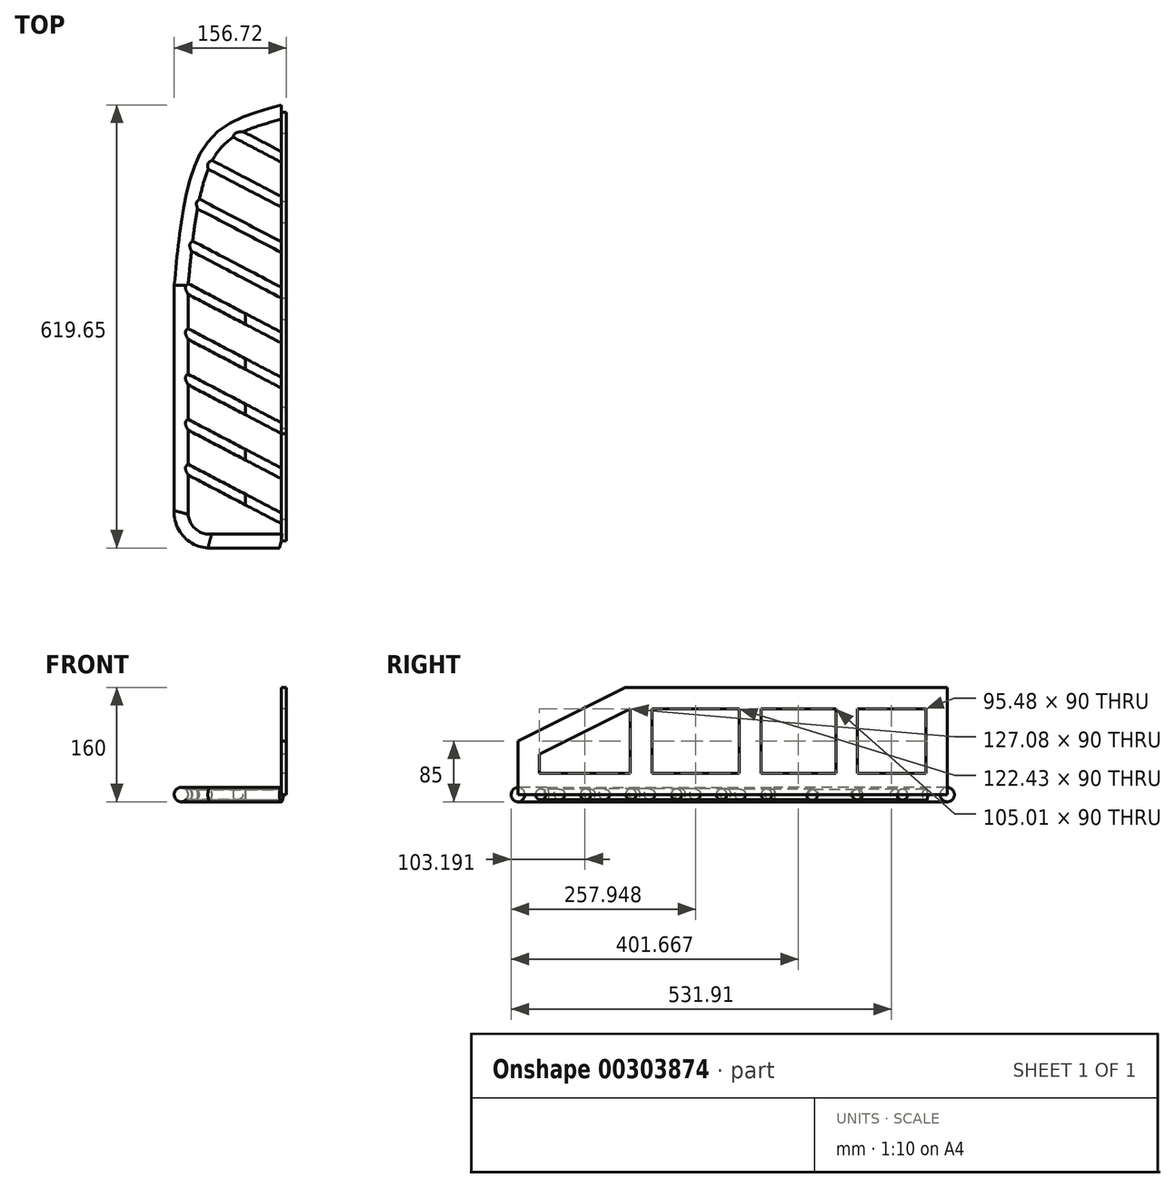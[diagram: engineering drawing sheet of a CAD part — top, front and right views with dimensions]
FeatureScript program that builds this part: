
annotation { "Feature Type Name" : "Feature", "Feature Type Description" : "" }
export const myFeature = defineFeature(function(context is Context, id is Id, definition is map)
    precondition{}
    {
        {
            var Q0;
            Q0=qCreatedBy(makeId("Right.planeOp"),FACE);
            var sketch = newSketch(context, id + "F0", { "sketchPlane" : qUnion([Q0])});
            skLineSegment(sketch, "E0.bottom", {"start": v(300, 75) * mm, "end": v(-150, 75) * mm});
            skLineSegment(sketch, "E0.top", {"start": v(300, -75) * mm, "end": v(-300, -75) * mm});
            skLineSegment(sketch, "E0.left", {"start": v(300, 75) * mm, "end": v(300, -75) * mm});
            skLineSegment(sketch, "E0.right", {"start": v(-300, 0) * mm, "end": v(-300, -75) * mm});
            skPoint(sketch, "E0.middle", {"position": v(0, 0) * mm});
            skLineSegment(sketch, "E1", {"start": v(-300, 0) * mm, "end": v(-150, 75) * mm});
            skLineSegment(sketch, "E2.0", {"start": v(-270, -18.54) * mm, "end": v(-142.92, 45) * mm});
            skLineSegment(sketch, "E2.1", {"start": v(270, 45) * mm, "end": v(174.52, 45) * mm});
            skLineSegment(sketch, "E2.2", {"start": v(-270, -18.54) * mm, "end": v(-270, -45) * mm});
            skLineSegment(sketch, "E2.3", {"start": v(270, -45) * mm, "end": v(174.52, -45) * mm});
            skLineSegment(sketch, "E2.4", {"start": v(270, 45) * mm, "end": v(270, -45) * mm});
            skLineSegment(sketch, "E3.left", {"start": v(-142.92, -45) * mm, "end": v(-142.92, 45) * mm});
            skLineSegment(sketch, "E3.right", {"start": v(-112.92, -45) * mm, "end": v(-112.92, 45) * mm});
            skLineSegment(sketch, "E4.left", {"start": v(9.51, -45) * mm, "end": v(9.51, 45) * mm});
            skLineSegment(sketch, "E4.right", {"start": v(39.51, -45) * mm, "end": v(39.51, 45) * mm});
            skLineSegment(sketch, "E5.left", {"start": v(144.52, 45) * mm, "end": v(144.52, -45) * mm});
            skLineSegment(sketch, "E5.right", {"start": v(174.52, 45) * mm, "end": v(174.52, -45) * mm});
            skLineSegment(sketch, "E6.trimOffspring", {"start": v(-142.92, -45) * mm, "end": v(-270, -45) * mm});
            skLineSegment(sketch, "E7.trimOffspring", {"start": v(9.51, -45) * mm, "end": v(-112.92, -45) * mm});
            skLineSegment(sketch, "E8.trimOffspring", {"start": v(9.51, 45) * mm, "end": v(-112.92, 45) * mm});
            skLineSegment(sketch, "E9.trimOffspring", {"start": v(144.52, 45) * mm, "end": v(39.51, 45) * mm});
            skLineSegment(sketch, "E10.trimOffspring", {"start": v(144.52, -45) * mm, "end": v(39.51, -45) * mm});
            skSolve(sketch);
        }
        {
            var Q0;
            Q0=makeQuery(id+"F0.imprint","IMPRINT",FACE,{"disambiguationData":[TD([[makeQuery(id+"F0.imprint","IMPRINT",EDGE,{"derivedFrom":sQuery(id+"F0.wireOp",EDGE,"E0.bottom")}),1.0]])]});
            extrude(context, id + "F1", {"entities" : qUnion([Q0]), "depth" : 7 * mm});
        }
        {
            var Q0;
            Q0=makeQuery(id+"F1.opExtrude","SWEPT_FACE",FACE,{"disambiguationData":[OSD([sQuery(id+"F0.wireOp",EDGE,"E0.top")])]});
            var sketch = newSketch(context, id + "F2", { "sketchPlane" : qUnion([Q0])});
            skLineSegment(sketch, "E11.bottom", {"start": v(0, 300) * mm, "end": v(-100, 300) * mm});
            skLineSegment(sketch, "E11.left", {"start": v(0, 300) * mm, "end": v(0, -300) * mm});
            skLineSegment(sketch, "E11.right", {"start": v(-140, 260) * mm, "end": v(-140, -57.71) * mm});
            skPoint(sketch, "E12.visualSharp", {"position": v(-140, 300) * mm});
            skArc(sketch, "E12.filletArc", {"start": v(-100, 300) * mm, "mid": v(-128.28, 288.28) * mm, "end": v(-140, 260) * mm});
            skFitSpline(sketch, "E13", {"points": [v(-140, -57.71) * mm, v(-122.28, -187.39) * mm, v(-83.71, -264.53) * mm, v(0, -300) * mm], "startDerivative": vector(33.93, -359.8) * mm, "endDerivative": vector(298.49, -80.87) * mm});
            skLineSegment(sketch, "E14", {"start": v(-100, 300) * mm, "end": v(-50, 242) * mm});
            skPoint(sketch, "E14.endSnap0", {"position": v(-50, 300) * mm});
            skLineSegment(sketch, "E15", {"start": v(-50, 242) * mm, "end": v(-140, 195) * mm});
            skLineSegment(sketch, "E16", {"start": v(-50, 242) * mm, "end": v(0, 268.12) * mm});
            skLineSegment(sketch, "E17", {"start": v(-140, 131.82) * mm, "end": v(0, 204.94) * mm});
            skLineSegment(sketch, "E18", {"start": v(-140, 68.64) * mm, "end": v(0, 141.76) * mm});
            skLineSegment(sketch, "E19", {"start": v(-140, 5.47) * mm, "end": v(0, 78.58) * mm});
            skLineSegment(sketch, "E20", {"start": v(-140, -57.71) * mm, "end": v(0, 15.4) * mm});
            skLineSegment(sketch, "E21", {"start": v(-133.86, -117.68) * mm, "end": v(0, -47.77) * mm});
            skLineSegment(sketch, "E22", {"start": v(-124.77, -176.11) * mm, "end": v(0, -110.95) * mm});
            skLineSegment(sketch, "E23", {"start": v(-108.11, -230.6) * mm, "end": v(0, -174.13) * mm});
            skLineSegment(sketch, "E24", {"start": v(0, -300) * mm, "end": v(-26.85, -251.33) * mm});
            skLineSegment(sketch, "E25", {"start": v(-70.54, -274.14) * mm, "end": v(0, -237.3) * mm});
            skSolve(sketch);
        }
        {
            var Q0;
            Q0=makeQuery(id+"F1.opExtrude","CAP_FACE",FACE,{"disambiguationData":[OSD([sQuery(id+"F0.wireOp",EDGE,"E0.bottom"),sQuery(id+"F0.wireOp",EDGE,"E0.top"),sQuery(id+"F0.wireOp",EDGE,"E0.left"),sQuery(id+"F0.wireOp",EDGE,"E0.right"),sQuery(id+"F0.wireOp",EDGE,"E1"),sQuery(id+"F0.wireOp",EDGE,"E2.0"),sQuery(id+"F0.wireOp",EDGE,"E2.1"),sQuery(id+"F0.wireOp",EDGE,"E2.2"),sQuery(id+"F0.wireOp",EDGE,"E2.3"),sQuery(id+"F0.wireOp",EDGE,"E2.4"),sQuery(id+"F0.wireOp",EDGE,"E3.left"),sQuery(id+"F0.wireOp",EDGE,"E3.right"),sQuery(id+"F0.wireOp",EDGE,"E4.left"),sQuery(id+"F0.wireOp",EDGE,"E4.right"),sQuery(id+"F0.wireOp",EDGE,"E5.left"),sQuery(id+"F0.wireOp",EDGE,"E5.right"),sQuery(id+"F0.wireOp",EDGE,"E6.trimOffspring"),sQuery(id+"F0.wireOp",EDGE,"E7.trimOffspring"),sQuery(id+"F0.wireOp",EDGE,"E8.trimOffspring"),sQuery(id+"F0.wireOp",EDGE,"E9.trimOffspring"),sQuery(id+"F0.wireOp",EDGE,"E10.trimOffspring")])],"isStart":true});
            var sketch = newSketch(context, id + "F3", { "sketchPlane" : qUnion([Q0])});
            skCircle(sketch, "E26", {"center": v(-300, -75) * mm, "radius": 10 * mm});
            skSolve(sketch);
        }
        {
            var Q0;
            {var subQ0=sQuery(id+"F3.wireOp",EDGE,"E26");var subQ1=makeQuery(id+"F1.opExtrude","CAP_EDGE",EDGE,{"disambiguationData":[OSD([sQuery(id+"F0.wireOp",EDGE,"E0.top")])],"isStart":true});var subQ2=makeQuery(id+"F3.imprint","INTERSECT",VERTEX,{"derivedFrom":[subQ1,subQ0]});Q0=makeQuery(id+"F3.imprint","IMPRINT",FACE,{"disambiguationData":[TD([[makeQuery(id+"F3.imprint","IMPRINT",EDGE,{"disambiguationData":[TD([[subQ2,1.0]])],"derivedFrom":subQ0}),1.0]])]});}
            var Q1;
            {var subQ0=sQuery(id+"F3.wireOp",EDGE,"E26");var subQ1=makeQuery(id+"F1.opExtrude","CAP_EDGE",EDGE,{"disambiguationData":[OSD([sQuery(id+"F0.wireOp",EDGE,"E0.top")])],"isStart":true});var subQ2=makeQuery(id+"F3.imprint","INTERSECT",VERTEX,{"derivedFrom":[subQ1,subQ0]});Q1=makeQuery(id+"F3.imprint","IMPRINT",FACE,{"disambiguationData":[TD([[makeQuery(id+"F3.imprint","IMPRINT",EDGE,{"disambiguationData":[TD([[subQ2,-1.0]])],"derivedFrom":subQ0}),1.0]])]});}
            var Q2;
            Q2=sQuery(id+"F2.wireOp",EDGE,"E13");
            var Q3;
            Q3=sQuery(id+"F2.wireOp",EDGE,"E11.right");
            var Q4;
            Q4=sQuery(id+"F2.wireOp",EDGE,"E12.filletArc");
            var Q5;
            Q5=sQuery(id+"F2.wireOp",EDGE,"E11.bottom");
            sweep(context, id + "F4", {"operationType" : NewBodyOperationType.ADD, "profiles" : qUnion([Q0, Q1]), "path" : qUnion([Q2, Q3, Q4, Q5])});
        }
        {
            var Q0;
            Q0=qCreatedBy(makeId("Right.planeOp"),FACE);
            var sketch = newSketch(context, id + "F5", { "sketchPlane" : qUnion([Q0])});
            skCircle(sketch, "E27", {"center": v(237.3, -75) * mm, "radius": 7.5 * mm});
            skCircle(sketch, "E28", {"center": v(174.46, -74.75) * mm, "radius": 7.5 * mm});
            skCircle(sketch, "E29", {"center": v(111.07, -75.43) * mm, "radius": 7.5 * mm});
            skCircle(sketch, "E30", {"center": v(47.44, -74.84) * mm, "radius": 7.5 * mm});
            skCircle(sketch, "E31", {"center": v(-15.46, -74.74) * mm, "radius": 7.5 * mm});
            skCircle(sketch, "E32", {"center": v(-78.5, -74.58) * mm, "radius": 7.5 * mm});
            skCircle(sketch, "E33", {"center": v(-142.03, -74.53) * mm, "radius": 7.5 * mm});
            skCircle(sketch, "E34", {"center": v(-205.31, -74.6) * mm, "radius": 7.5 * mm});
            skCircle(sketch, "E35", {"center": v(-268.15, -74.7) * mm, "radius": 7.5 * mm});
            skSolve(sketch);
        }
        {
            var Q0;
            Q0=makeQuery(id+"F5.imprint","IMPRINT",FACE,{"disambiguationData":[TD([[makeQuery(id+"F5.imprint","IMPRINT",EDGE,{"derivedFrom":sQuery(id+"F5.wireOp",EDGE,"E27")}),1.0]])]});
            var Q1;
            Q1=sQuery(id+"F2.wireOp",EDGE,"E25");
            sweep(context, id + "F6", {"operationType" : NewBodyOperationType.ADD, "profiles" : qUnion([Q0]), "path" : qUnion([Q1])});
        }
        {
            var Q0;
            Q0=makeQuery(id+"F5.imprint","IMPRINT",FACE,{"disambiguationData":[TD([[makeQuery(id+"F5.imprint","IMPRINT",EDGE,{"derivedFrom":sQuery(id+"F5.wireOp",EDGE,"E35")}),1.0]])]});
            var Q1;
            Q1=makeQuery(id+"F5.imprint","IMPRINT",FACE,{"disambiguationData":[TD([[makeQuery(id+"F5.imprint","IMPRINT",EDGE,{"derivedFrom":sQuery(id+"F5.wireOp",EDGE,"E34")}),1.0]])]});
            var Q2;
            Q2=makeQuery(id+"F5.imprint","IMPRINT",FACE,{"disambiguationData":[TD([[makeQuery(id+"F5.imprint","IMPRINT",EDGE,{"derivedFrom":sQuery(id+"F5.wireOp",EDGE,"E33")}),1.0]])]});
            var Q3;
            Q3=makeQuery(id+"F5.imprint","IMPRINT",FACE,{"disambiguationData":[TD([[makeQuery(id+"F5.imprint","IMPRINT",EDGE,{"derivedFrom":sQuery(id+"F5.wireOp",EDGE,"E32")}),1.0]])]});
            var Q4;
            Q4=makeQuery(id+"F5.imprint","IMPRINT",FACE,{"disambiguationData":[TD([[makeQuery(id+"F5.imprint","IMPRINT",EDGE,{"derivedFrom":sQuery(id+"F5.wireOp",EDGE,"E31")}),1.0]])]});
            var Q5;
            Q5=sQuery(id+"F2.wireOp",EDGE,"E16");
            var Q6;
            Q6=sQuery(id+"F2.wireOp",EDGE,"E15");
            sweep(context, id + "F7", {"operationType" : NewBodyOperationType.ADD, "profiles" : qUnion([Q0, Q1, Q2, Q3, Q4]), "path" : qUnion([Q5, Q6])});
        }
        {
            var Q0;
            Q0=makeQuery(id+"F5.imprint","IMPRINT",FACE,{"disambiguationData":[TD([[makeQuery(id+"F5.imprint","IMPRINT",EDGE,{"derivedFrom":sQuery(id+"F5.wireOp",EDGE,"E30")}),1.0]])]});
            var Q1;
            Q1=sQuery(id+"F2.wireOp",EDGE,"E21");
            sweep(context, id + "F8", {"operationType" : NewBodyOperationType.ADD, "profiles" : qUnion([Q0]), "path" : qUnion([Q1])});
        }
        {
            var Q0;
            Q0=makeQuery(id+"F5.imprint","IMPRINT",FACE,{"disambiguationData":[TD([[makeQuery(id+"F5.imprint","IMPRINT",EDGE,{"derivedFrom":sQuery(id+"F5.wireOp",EDGE,"E29")}),1.0]])]});
            var Q1;
            Q1=sQuery(id+"F2.wireOp",EDGE,"E22");
            sweep(context, id + "F9", {"operationType" : NewBodyOperationType.ADD, "profiles" : qUnion([Q0]), "path" : qUnion([Q1])});
        }
        {
            var Q0;
            Q0=makeQuery(id+"F5.imprint","IMPRINT",FACE,{"disambiguationData":[TD([[makeQuery(id+"F5.imprint","IMPRINT",EDGE,{"derivedFrom":sQuery(id+"F5.wireOp",EDGE,"E28")}),1.0]])]});
            var Q1;
            Q1=sQuery(id+"F2.wireOp",EDGE,"E23");
            sweep(context, id + "F10", {"operationType" : NewBodyOperationType.ADD, "profiles" : qUnion([Q0]), "path" : qUnion([Q1])});
        }
    });
